# Revit family: Cabinet-Overhead-Teknion-BOSG-Sliding_Glass_Doors-R2015
name_source: partatom
category: Casework
revit_build: Autodesk Revit Architecture 2015 (Build: 20140323_1530(x64)
units: mm (PartAtom-declared; Revit-internal decimal feet)

## types (2) — shared parameters
Assembly Code = E2020200
Description = Overhead Cabinet - Glass Sliding Doors, 16"Depth x 15" High, Wall Panel Mounted
Manufacturer = Teknion
Manufacturer Fax = 416.661.4586
Model = BOSGW16_15
Part Number = BOSG
Product Documentation Link = http://www.teknion.com
Product Line = Expansion Casegoods
Product Page URL = http://www.teknion.com
Series = Expansion Casegoods
Sustainability Data = http://www.teknion.com
URL = http://www.teknion.com
Unit Weight URL = http://www.teknion.com
Warranty = http://www.teknion.com

## per-type parameters (varying)
| type | Height |
| 66" Mounting Height | 51.508 " |
| 72" Mounting Height | 57.76 " |

## geometry (parser evidence)
native form markers: Blend x139, Sweep x2
no freeform markers — native parametric forms only
